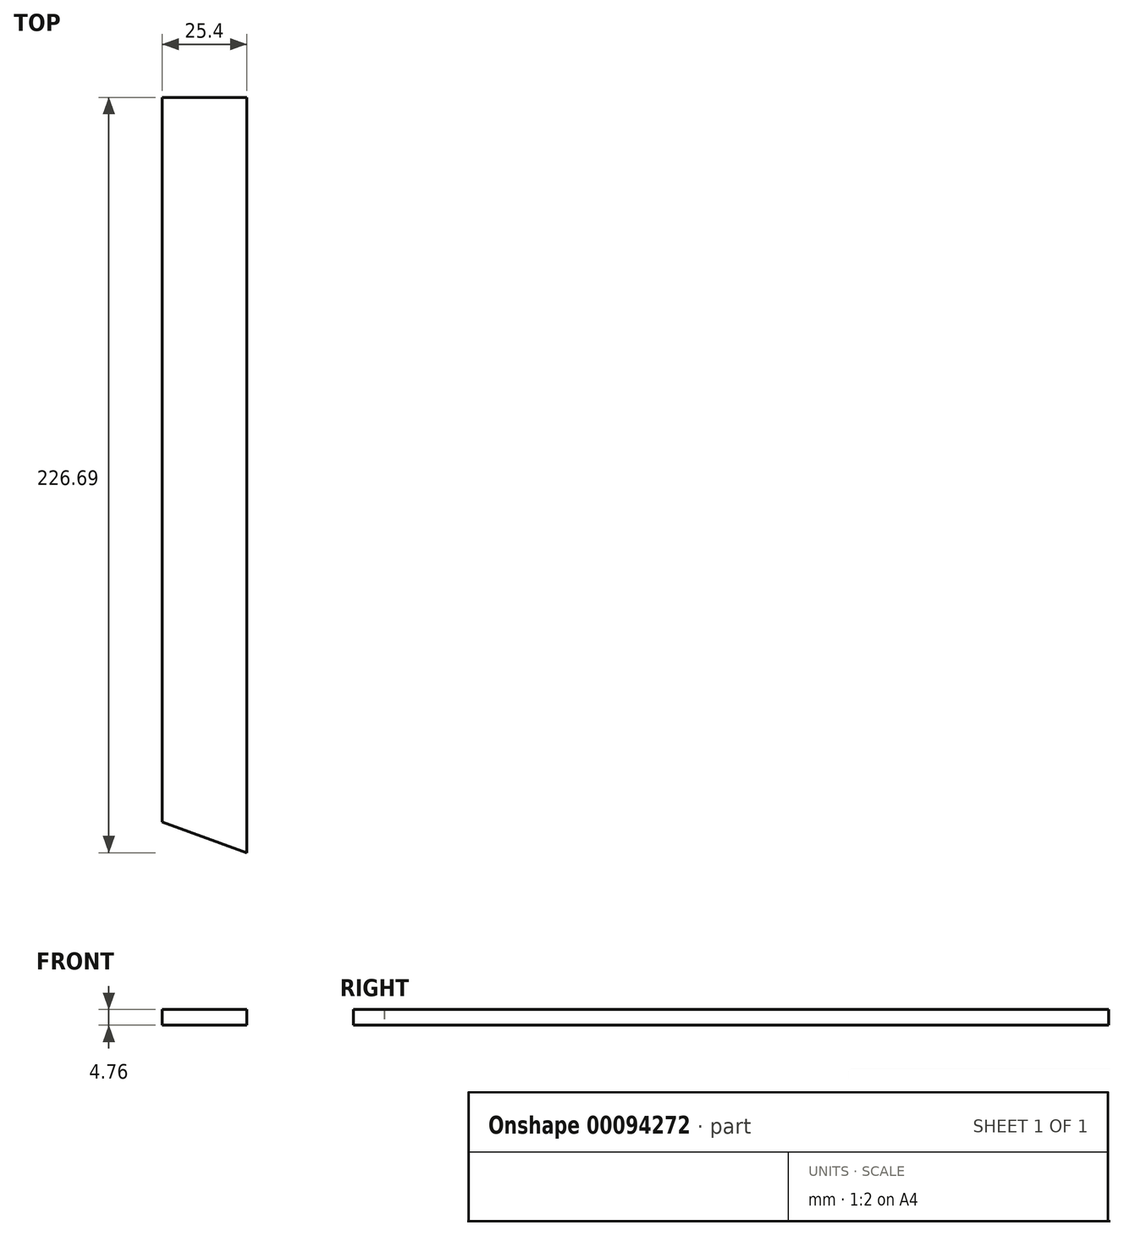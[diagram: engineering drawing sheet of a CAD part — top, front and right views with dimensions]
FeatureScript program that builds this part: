
annotation { "Feature Type Name" : "Feature", "Feature Type Description" : "" }
export const myFeature = defineFeature(function(context is Context, id is Id, definition is map)
    precondition{}
    {
        {
            var Q0;
            Q0=qCreatedBy(makeId("Top.planeOp"),FACE);
            var sketch = newSketch(context, id + "F0", { "sketchPlane" : qUnion([Q0])});
            skLineSegment(sketch, "E0.bottom", {"start": v(12.7, 108.72) * mm, "end": v(-12.7, 108.72) * mm});
            skLineSegment(sketch, "E0.right", {"start": v(-12.7, 108.72) * mm, "end": v(-12.7, -108.72) * mm});
            skPoint(sketch, "E0.middle", {"position": v(0, 0) * mm});
            skPoint(sketch, "E1.end.orphan", {"position": v(12.7, -108.72) * mm});
            skLineSegment(sketch, "E2", {"start": v(12.7, 108.72) * mm, "end": v(12.7, -117.97) * mm});
            skLineSegment(sketch, "E3", {"start": v(-12.7, -108.72) * mm, "end": v(12.7, -117.97) * mm});
            skSolve(sketch);
        }
        {
            var Q0;
            Q0 = qSketchRegion(id + "F0", true);
            extrude(context, id + "F1", {"entities" : qUnion([Q0]), "depth" : 4.76 * mm});
        }
    });
